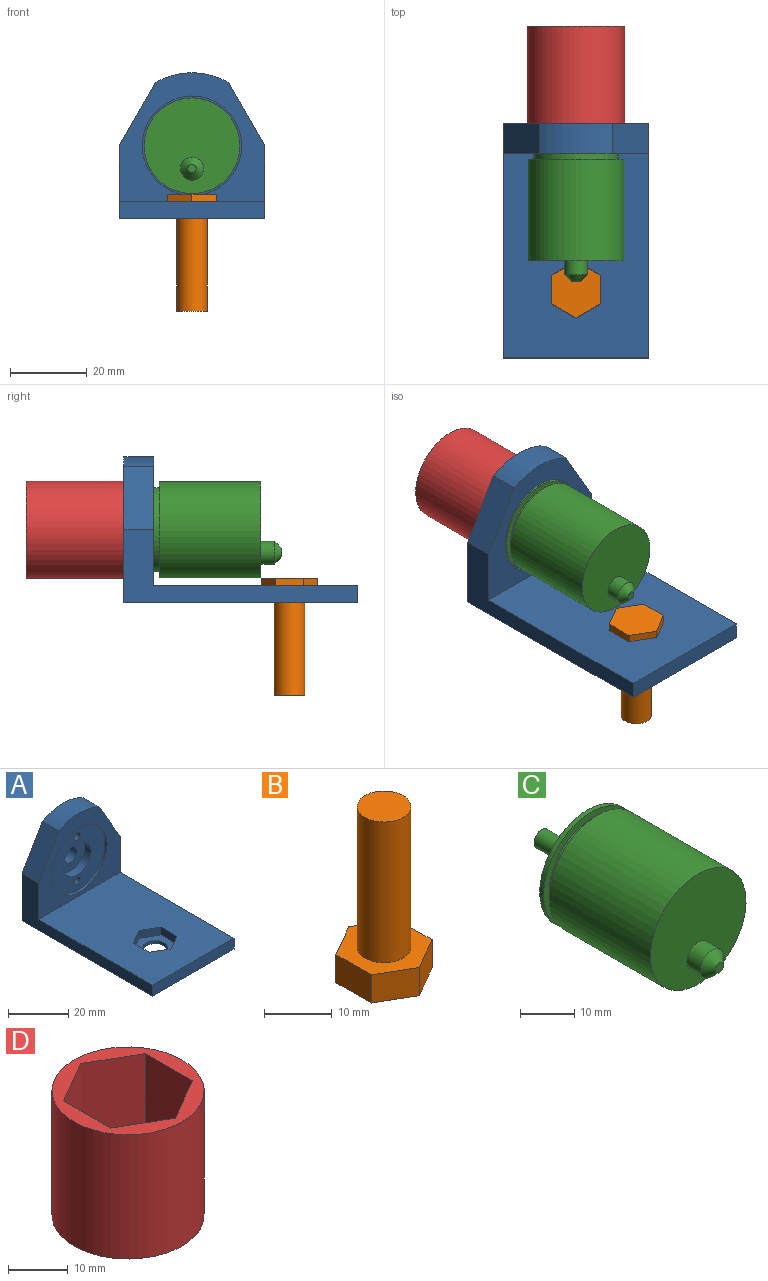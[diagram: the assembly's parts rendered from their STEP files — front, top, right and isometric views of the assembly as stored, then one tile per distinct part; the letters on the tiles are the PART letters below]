
ASSEMBLY  parts=4 mates=3
PART A: 25 faces, bbox 38.1x61.1x38.1 mm
  f0: plane 53.34x38.1mm, normal (0,0,1), area 1886.9mm2, adj f1,f3,f7,f8,f9,f10,f11,f12
  f1: plane 61.12x19.05mm, normal (-1,0,0), area 385.3mm2, adj f0,f2,f6,f7,f8,f17
  f2: plane 61.12x38.1mm, normal (0,0,-1), area 2278.3mm2, adj f1,f3,f8,f16,f17
  f3: plane 61.12x19.05mm, normal (1,0,0), area 385.3mm2, adj f0,f2,f4,f7,f8,f17
  f4: plane 16.5x9.53mm, normal (0.87,0,0.5), area 148.2mm2, adj f3,f5,f7,f17
  f5: cylinder r=19.05mm len=19.05mm, axis (0,1,0), area 155.2mm2, adj f4,f6,f7,f17
  f6: plane 16.5x9.53mm, normal (-0.87,0,0.5), area 148.2mm2, adj f1,f5,f7,f17
  f7: plane 38.1x33.66mm, normal (0,-1,0), area 529.8mm2, adj f0,f1,f3,f4,f5,f6,f18
  f8: plane 38.1x4.45mm, normal (0,-1,0), area 169.4mm2, adj f0,f1,f2,f3
  f9: plane 6.48x3.74mm, normal (-0.5,-0.87,0), area 23.7mm2, adj f0,f10,f14,f15
  f10: plane 6.48x3.74mm, normal (0.5,-0.87,0), area 23.7mm2, adj f0,f9,f11,f15
  f11: plane 7.48x3.18mm, normal (1,0,0), area 23.7mm2, adj f0,f10,f12,f15
  f12: plane 6.48x3.74mm, normal (0.5,0.87,0), area 23.7mm2, adj f0,f11,f13,f15
  f13: plane 6.48x3.74mm, normal (-0.5,0.87,0), area 23.7mm2, adj f0,f12,f14,f15
  f14: plane 7.48x3.18mm, normal (-1,0,0), area 23.7mm2, adj f0,f9,f13,f15
  f15: plane 14.96x12.95mm, normal (0,0,1), area 95mm2, adj f9,f10,f11,f12,f13,f14,f16
  f16: cylinder r=4mm len=8mm, axis (0,0,1), area 31.9mm2, adj f2,f15
  f17: plane 38.1x38.1mm, normal (0,1,0), area 1187.7mm2, adj f1,f2,f3,f4,f5,f6,f22,f23
  f18: cylinder r=13mm len=26mm, axis (0,-1,0), area 81.7mm2, adj f7,f19
  f19: plane 26x26mm, normal (0,-1,0), area 384.1mm2, adj f18,f20,f23,f24
  f20: cylinder r=6.5mm len=13mm, axis (0,-1,0), area 122.5mm2, adj f19,f21
  f21: plane 13x13mm, normal (0,-1,0), area 104.5mm2, adj f20,f22
  f22: cylinder r=3mm len=6mm, axis (0,-1,0), area 71.2mm2, adj f17,f21
  f23: cylinder r=1.5mm len=6.78mm, axis (0,-1,0), area 63.9mm2, adj f17,f19
  f24: cylinder r=1.5mm len=6.78mm, axis (0,-1,0), area 63.9mm2, adj f17,f19
PART B: 10 faces, bbox 12.7x14.7x30.5 mm
  f0: plane 7.33x5.08mm, normal (1,0,0), area 37.2mm2, adj f1,f5,f6,f7
  f1: plane 6.35x5.08mm, normal (0.5,0.87,0), area 37.2mm2, adj f0,f2,f6,f7
  f2: plane 6.35x5.08mm, normal (-0.5,0.87,0), area 37.2mm2, adj f1,f3,f6,f7
  f3: plane 7.33x5.08mm, normal (-1,0,0), area 37.2mm2, adj f2,f4,f6,f7
  f4: plane 6.35x5.08mm, normal (-0.5,-0.87,0), area 37.2mm2, adj f3,f5,f6,f7
  f5: plane 6.35x5.08mm, normal (0.5,-0.87,0), area 37.2mm2, adj f0,f4,f6,f7
  f6: plane 14.66x12.7mm, normal (0,0,1), area 90.2mm2, adj f0,f1,f2,f3,f4,f5,f8
  f7: plane 14.66x12.7mm, normal (0,0,-1), area 139.7mm2, adj f0,f1,f2,f3,f4,f5
  f8: cylinder r=3.97mm len=25.4mm, axis (0,0,-1), area 633.4mm2, adj f6,f9
  f9: plane 7.94x7.94mm, normal (0,0,1), area 49.5mm2, adj f8
PART C: 18 faces, bbox 25x46.5x25 mm
  f0: plane 25x25mm, normal (0,1,0), area 363.6mm2, adj f1,f10,f12,f14
  f1: cylinder r=6mm len=12mm, axis (0,1,0), area 75.4mm2, adj f0,f2
  f2: plane 12x12mm, normal (0,1,0), area 100.5mm2, adj f1,f3
  f3: cylinder r=2mm len=10mm, axis (0,1,0), area 125.7mm2, adj f2,f4
  f4: plane 4x4mm, normal (0,1,0), area 12.6mm2, adj f3
  f5: plane 25x25mm, normal (0,-1,0), area 462.6mm2, adj f6,f15
  f6: cylinder r=12.5mm len=26.5mm, axis (0,1,0), area 2081.3mm2, adj f5,f7
  f7: plane 25x25mm, normal (0,1,0), area 110.7mm2, adj f6,f8
  f8: cylinder r=11mm len=22mm, axis (0,1,0), area 103.7mm2, adj f7,f9
  f9: plane 25x25mm, normal (0,-1,0), area 110.7mm2, adj f8,f10
  f10: cylinder r=12.5mm len=25mm, axis (0,1,0), area 78.5mm2, adj f0,f9
  f11: cone r=0mm half-angle=59deg, axis (0,1,0), area 8.2mm2, adj f12
  f12: cylinder r=1.5mm len=4mm, axis (0,1,0), area 37.7mm2, adj f0,f11
  f13: cone r=0mm half-angle=59deg, axis (0,1,0), area 8.2mm2, adj f14
  f14: cylinder r=1.5mm len=4mm, axis (0,1,0), area 37.7mm2, adj f0,f13
  f15: cylinder r=3mm len=6mm, axis (0,1,0), area 67.8mm2, adj f5,f17
  f16: plane 2.19x2.19mm, normal (0,-1,0), area 3.8mm2, adj f17
  f17: cone r=1.09mm half-angle=45deg, axis (0,1,0), area 34.7mm2, adj f15,f16
PART D: 11 faces, bbox 25.4x25.4x25.4 mm
  f0: plane 15.24x9.65mm, normal (-0.5,-0.87,0), area 169.9mm2, adj f1,f6,f7,f10
  f1: plane 15.24x11.15mm, normal (-1,0,0), area 169.9mm2, adj f0,f2,f7,f10
  f2: plane 15.24x9.65mm, normal (-0.5,0.87,0), area 169.9mm2, adj f1,f3,f7,f10
  f3: plane 15.24x9.65mm, normal (0.5,0.87,0), area 169.9mm2, adj f2,f4,f7,f10
  f4: plane 15.24x11.15mm, normal (1,0,0), area 169.9mm2, adj f3,f6,f7,f10
  f5: cylinder r=12.7mm len=25.4mm, axis (0,0,-1), area 2026.8mm2, adj f7,f8
  f6: plane 15.24x9.65mm, normal (0.5,-0.87,0), area 169.9mm2, adj f0,f4,f7,f10
  f7: plane 25.4x25.4mm, normal (0,0,1), area 184mm2, adj f0,f1,f2,f3,f4,f5,f6
  f8: plane 25.4x25.4mm, normal (0,0,-1), area 492.5mm2, adj f5,f9
  f9: cylinder r=2.12mm len=10.16mm, axis (0,0,-1), area 135.7mm2, adj f8,f10
  f10: plane 22.29x19.3mm, normal (0,0,1), area 308.5mm2, adj f0,f1,f2,f3,f4,f6,f9
PLACE A at identity
PLACE B rot(axis=(1,0,0),180deg) t=(0,-39.29,-8.71)mm
PLACE C t=(0,-31.81,3.99)mm
PLACE D rot(axis=(-1,0,0),90deg) t=(0,4.11,3.99)mm
MATE slider D.f9 <-> C.f1  axis (0,-1,0) through (0,4.11,3.99)mm
MATE fastened C.f1 <-> A.f5  axis (0,-1,0) through (0,-3.81,3.99)mm
MATE fastened B.f8 <-> A.f16  axis (0,0,-1) through (0,-39.29,-13.79)mm
